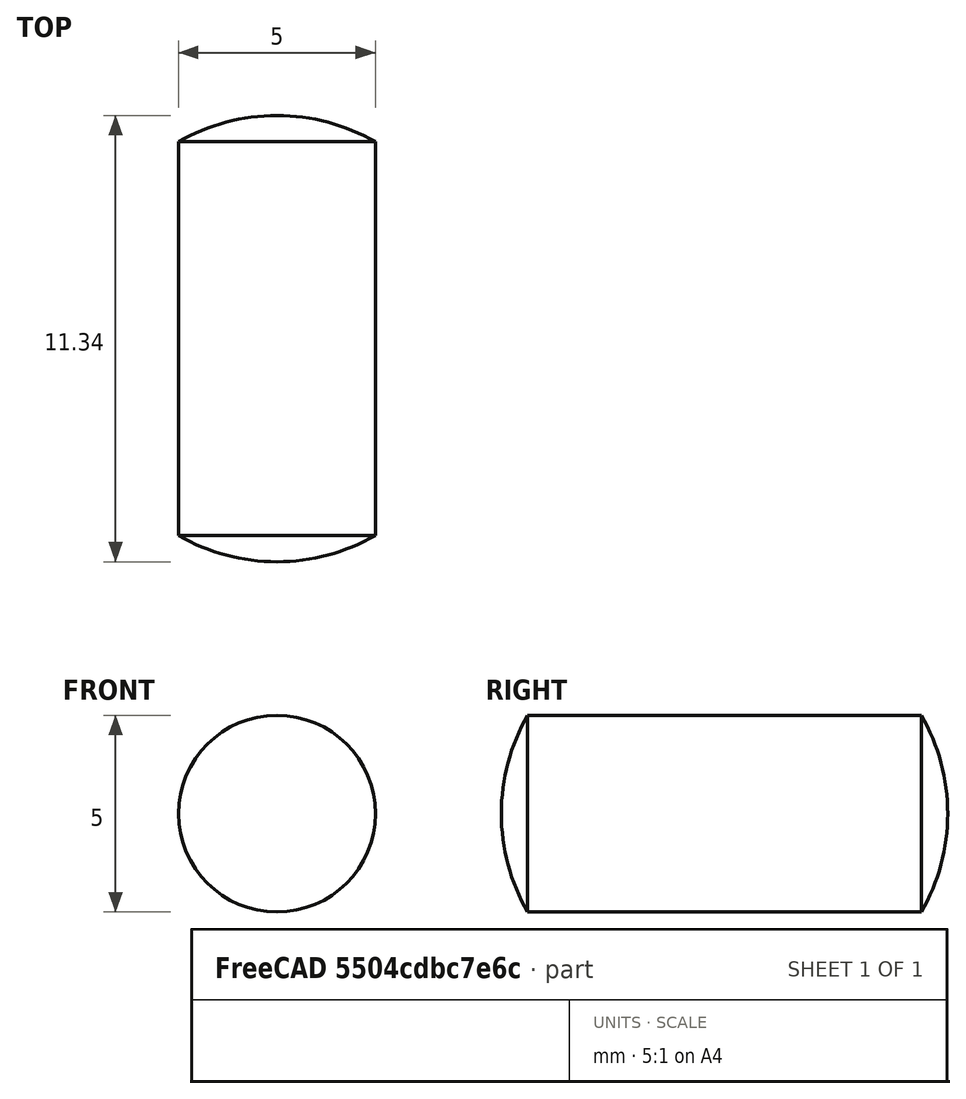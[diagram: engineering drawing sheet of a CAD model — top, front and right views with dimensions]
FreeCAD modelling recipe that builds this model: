
FCSTD DOCUMENT  (FreeCAD 0.15R4470 (Git))
Label: Zyl-Stift_DIN_7-5x10
License: CC-BY 3.0
LicenseURL: http://creativecommons.org/licenses/by/3.0/
objects: Sketcher::SketchObject×1, PartDesign::Revolution×1
note: 3 computed .brp shape members not serialized (recipe doc carries the construction recipe); baked Part::Feature solids carry a one-line shape summary decoded from their .brp

FEATURE [Sketcher::SketchObject] Sketch
  Placement = pos=(0,0,0) rot=(0.57735,0.57735,0.57735;2.0944rad)
  sketch-geometry (4):
    g0: ArcOfCircle CenterX=5.66987 CenterY=0 CenterZ=0 NormalX=0 NormalY=0 NormalZ=1 Radius=5 StartAngle=0 EndAngle=0.523599
    g1: LineSegment StartX=-3e-12 StartY=2.5 StartZ=0 EndX=10 EndY=2.5 EndZ=0
    g2: LineSegment StartX=-0.669873 StartY=0 StartZ=0 EndX=10.6699 EndY=0 EndZ=0
    g3: ArcOfCircle CenterX=4.33013 CenterY=0 CenterZ=0 NormalX=0 NormalY=0 NormalZ=1 Radius=5 StartAngle=2.61799 EndAngle=3.14159
  constraints (14):
    c: PointOnObject(g2,g-1)
    c: PointOnObject(g1,g-2)
    c: Coincident(g0,g1)
    c: PointOnObject(g0,g-1)
    c: Horizontal(g1)
    c: Coincident(g2,g0)
    c: Horizontal(g2)
    c: Radius(g0) = 5
    c: PointOnObject(g3,g2)
    c: Coincident(g3,g1)
    c: Coincident(g3,g2)
    c: Equal(g3,g0)
    c: DistanceY(g-1,g1) = 2.5
    c: DistanceX(g1) = 10
FEATURE [PartDesign::Revolution] Revolution  label="Zyl-Stift DIN 7-5x10 #"
  Angle = 360
  Axis = (0,1,0)
  Base = (0,0,0)
  Placement = pos=(0,0,0) rot=(0.57735,0.57735,0.57735;2.0944rad)
  ReferenceAxis = -> Sketch [H_Axis]
  Sketch = -> Sketch
